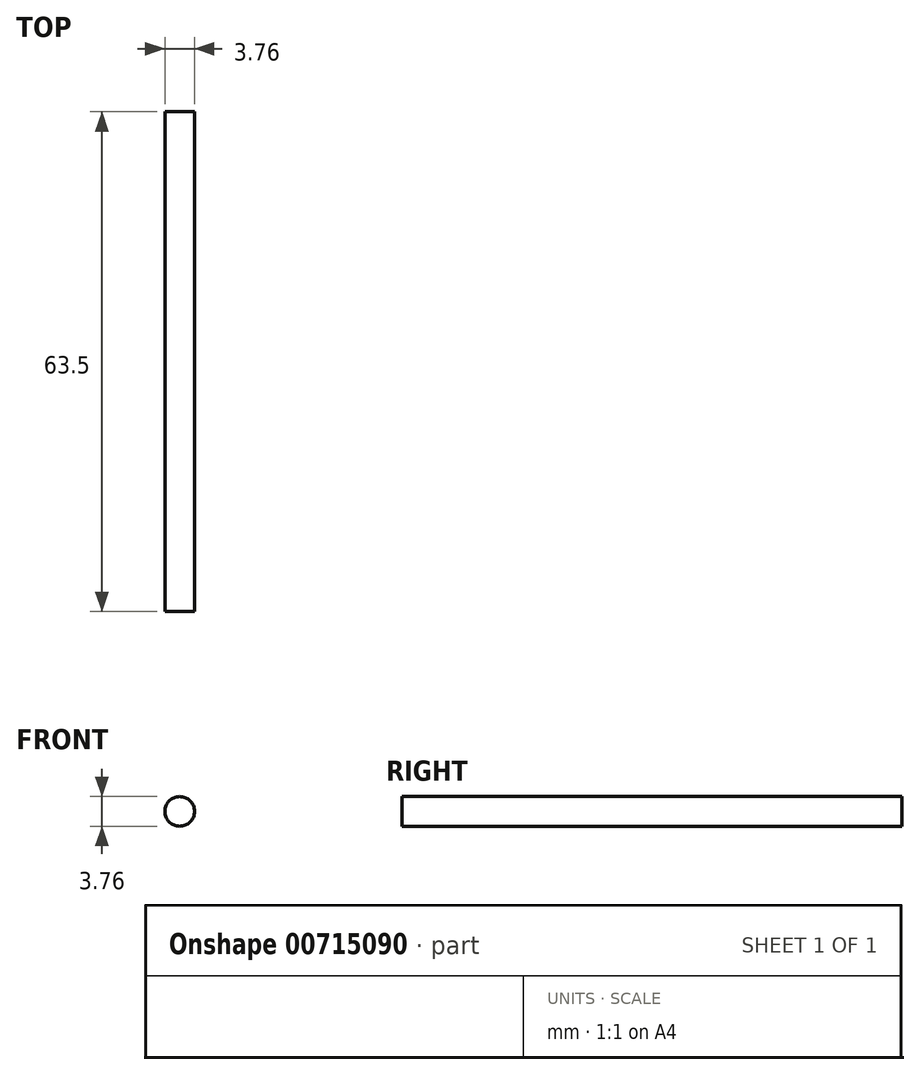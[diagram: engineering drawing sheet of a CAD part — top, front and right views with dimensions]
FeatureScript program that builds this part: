
annotation { "Feature Type Name" : "Feature", "Feature Type Description" : "" }
export const myFeature = defineFeature(function(context is Context, id is Id, definition is map)
    precondition{}
    {
        {
            var Q0;
            Q0=qCreatedBy(makeId("Front.planeOp"),FACE);
            var sketch = newSketch(context, id + "F0", { "sketchPlane" : qUnion([Q0])});
            skCircle(sketch, "E0", {"center": v(0, 0) * mm, "radius": 1.88 * mm});
            skSolve(sketch);
        }
        {
            var Q0;
            Q0 = qSketchRegion(id + "F0", true);
            extrude(context, id + "F1", {"entities" : qUnion([Q0]), "depth" : 63.5 * mm, "offsetDistance" : 25.4 * mm});
        }
    });
